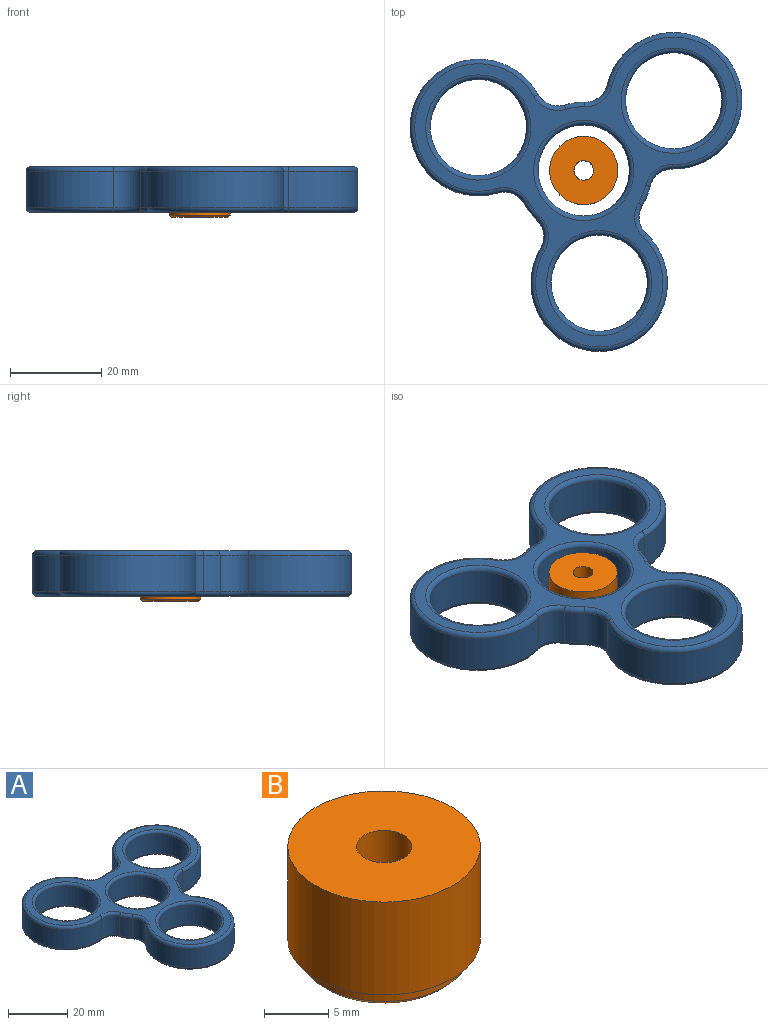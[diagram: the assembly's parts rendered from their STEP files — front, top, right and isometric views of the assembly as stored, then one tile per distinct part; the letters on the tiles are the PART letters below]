
ASSEMBLY  parts=2 mates=1
PART A: 50 faces, bbox 75.8x70x10 mm
  f0: cylinder r=15mm len=8mm, axis (0,0,-1), area 36.4mm2, adj f12,f17,f28,f39
  f1: cylinder r=15mm len=30mm, axis (0,0,-1), area 539mm2, adj f12,f13,f24,f35
  f2: cylinder r=15mm len=8mm, axis (0,0,-1), area 36.4mm2, adj f13,f14,f20,f31
  f3: cylinder r=15mm len=30mm, axis (0,0,-1), area 539mm2, adj f14,f15,f19,f32
  f4: cylinder r=15mm len=8mm, axis (0,0,-1), area 36.4mm2, adj f15,f16,f23,f36
  f5: cylinder r=10.56mm len=21.12mm, axis (0,0,-1), area 530.8mm2, adj f43,f48
  f6: cylinder r=10mm len=20mm, axis (0,0,-1), area 502.7mm2, adj f44,f47
  f7: cylinder r=15mm len=30mm, axis (0,0,-1), area 539mm2, adj f16,f17,f27,f40
  f8: cylinder r=10.56mm len=21.12mm, axis (0,0,-1), area 530.8mm2, adj f45,f46
  f9: cylinder r=10.56mm len=21.12mm, axis (0,0,-1), area 530.8mm2, adj f42,f49
  f10: plane 71.3x65.5mm, normal (0,0,1), area 795.3mm2, adj f18,f19,f20,f21,f22,f23,f24,f25
  f11: plane 71.3x65.5mm, normal (0,0,-1), area 795.3mm2, adj f30,f31,f32,f33,f34,f35,f36,f37
  f12: cylinder r=5mm len=8mm, axis (0,0,1), area 54mm2, adj f0,f1,f26,f37
  f13: cylinder r=5mm len=8mm, axis (0,0,1), area 54mm2, adj f1,f2,f22,f33
  f14: cylinder r=5mm len=8mm, axis (0,0,1), area 54mm2, adj f2,f3,f18,f30
  f15: cylinder r=5mm len=8mm, axis (0,0,1), area 54mm2, adj f3,f4,f21,f34
  f16: cylinder r=5mm len=8mm, axis (0,0,1), area 54mm2, adj f4,f7,f25,f38
  f17: cylinder r=5mm len=8mm, axis (0,0,1), area 54mm2, adj f0,f7,f29,f41
  f18: torus R=6mm, axis (0,0,1), area 11.4mm2, adj f10,f14,f19,f20
  f19: torus R=14mm, axis (0,0,1), area 103.3mm2, adj f3,f10,f18,f21
  f20: torus R=14mm, axis (0,0,1), area 7mm2, adj f2,f10,f18,f22
  f21: torus R=6mm, axis (0,0,1), area 11.4mm2, adj f10,f15,f19,f23
  f22: torus R=6mm, axis (0,0,1), area 11.4mm2, adj f10,f13,f20,f24
  f23: torus R=14mm, axis (0,0,1), area 7mm2, adj f4,f10,f21,f25
  f24: torus R=14mm, axis (0,0,1), area 103.3mm2, adj f1,f10,f22,f26
  f25: torus R=6mm, axis (0,0,1), area 11.4mm2, adj f10,f16,f23,f27
  f26: torus R=6mm, axis (0,0,1), area 11.4mm2, adj f10,f12,f24,f28
  f27: torus R=14mm, axis (0,0,1), area 103.3mm2, adj f7,f10,f25,f29
  f28: torus R=14mm, axis (0,0,1), area 7mm2, adj f0,f10,f26,f29
  f29: torus R=6mm, axis (0,0,1), area 11.4mm2, adj f10,f17,f27,f28
  f30: torus R=6mm, axis (0,0,1), area 11.4mm2, adj f11,f14,f31,f32
  f31: torus R=14mm, axis (0,0,1), area 7mm2, adj f2,f11,f30,f33
  f32: torus R=14mm, axis (0,0,1), area 103.3mm2, adj f3,f11,f30,f34
  f33: torus R=6mm, axis (0,0,1), area 11.4mm2, adj f11,f13,f31,f35
  f34: torus R=6mm, axis (0,0,1), area 11.4mm2, adj f11,f15,f32,f36
  f35: torus R=14mm, axis (0,0,1), area 103.3mm2, adj f1,f11,f33,f37
  f36: torus R=14mm, axis (0,0,1), area 7mm2, adj f4,f11,f34,f38
  f37: torus R=6mm, axis (0,0,1), area 11.4mm2, adj f11,f12,f35,f39
  f38: torus R=6mm, axis (0,0,1), area 11.4mm2, adj f11,f16,f36,f40
  f39: torus R=14mm, axis (0,0,1), area 7mm2, adj f0,f11,f37,f41
  f40: torus R=14mm, axis (0,0,1), area 103.3mm2, adj f7,f11,f38,f41
  f41: torus R=6mm, axis (0,0,1), area 11.4mm2, adj f11,f17,f39,f40
  f42: torus R=11.56mm, axis (0,0,1), area 107.8mm2, adj f9,f11
  f43: torus R=11.56mm, axis (0,0,1), area 107.8mm2, adj f5,f11
  f44: torus R=11mm, axis (0,0,1), area 102.3mm2, adj f6,f11
  f45: torus R=11.56mm, axis (0,0,1), area 107.8mm2, adj f8,f11
  f46: torus R=11.56mm, axis (0,0,1), area 107.8mm2, adj f8,f10
  f47: torus R=11mm, axis (0,0,1), area 102.3mm2, adj f6,f10
  f48: torus R=11.56mm, axis (0,0,1), area 107.8mm2, adj f5,f10
  f49: torus R=11.56mm, axis (0,0,1), area 107.8mm2, adj f9,f10
PART B: 9 faces, bbox 15x15x10.6 mm
  f0: cylinder r=7.5mm len=15mm, axis (0,0,-1), area 417.5mm2, adj f2,f3
  f1: cylinder r=2.17mm len=8.86mm, axis (0,0,-1), area 120.8mm2, adj f2,f7
  f2: plane 15x15mm, normal (0,0,1), area 161.9mm2, adj f0,f1
  f3: plane 15x15mm, normal (0,0,-1), area 37.3mm2, adj f0,f4
  f4: cylinder r=6.66mm len=13.32mm, axis (0,0,1), area 50.6mm2, adj f3,f8
  f5: cylinder r=2.12mm len=4.25mm, axis (0,0,1), area 22.9mm2, adj f6,f7
  f6: plane 12.31x12.31mm, normal (0,0,-1), area 104.8mm2, adj f5,f8
  f7: plane 4.34x4.34mm, normal (0,0,1), area 0.6mm2, adj f1,f5
  f8: cone r=6.66mm half-angle=45deg, axis (0,0,1), area 28.9mm2, adj f4,f6
PLACE A rot(axis=(0,0,-1),112.2deg) t=(-1.29,-3.41,-0.57)mm
PLACE B t=(-1.29,-3.41,0)mm
MATE revolute A.f4 <-> B.f1  axis (0,0,-1) through (-1.29,-3.41,4.43)mm
